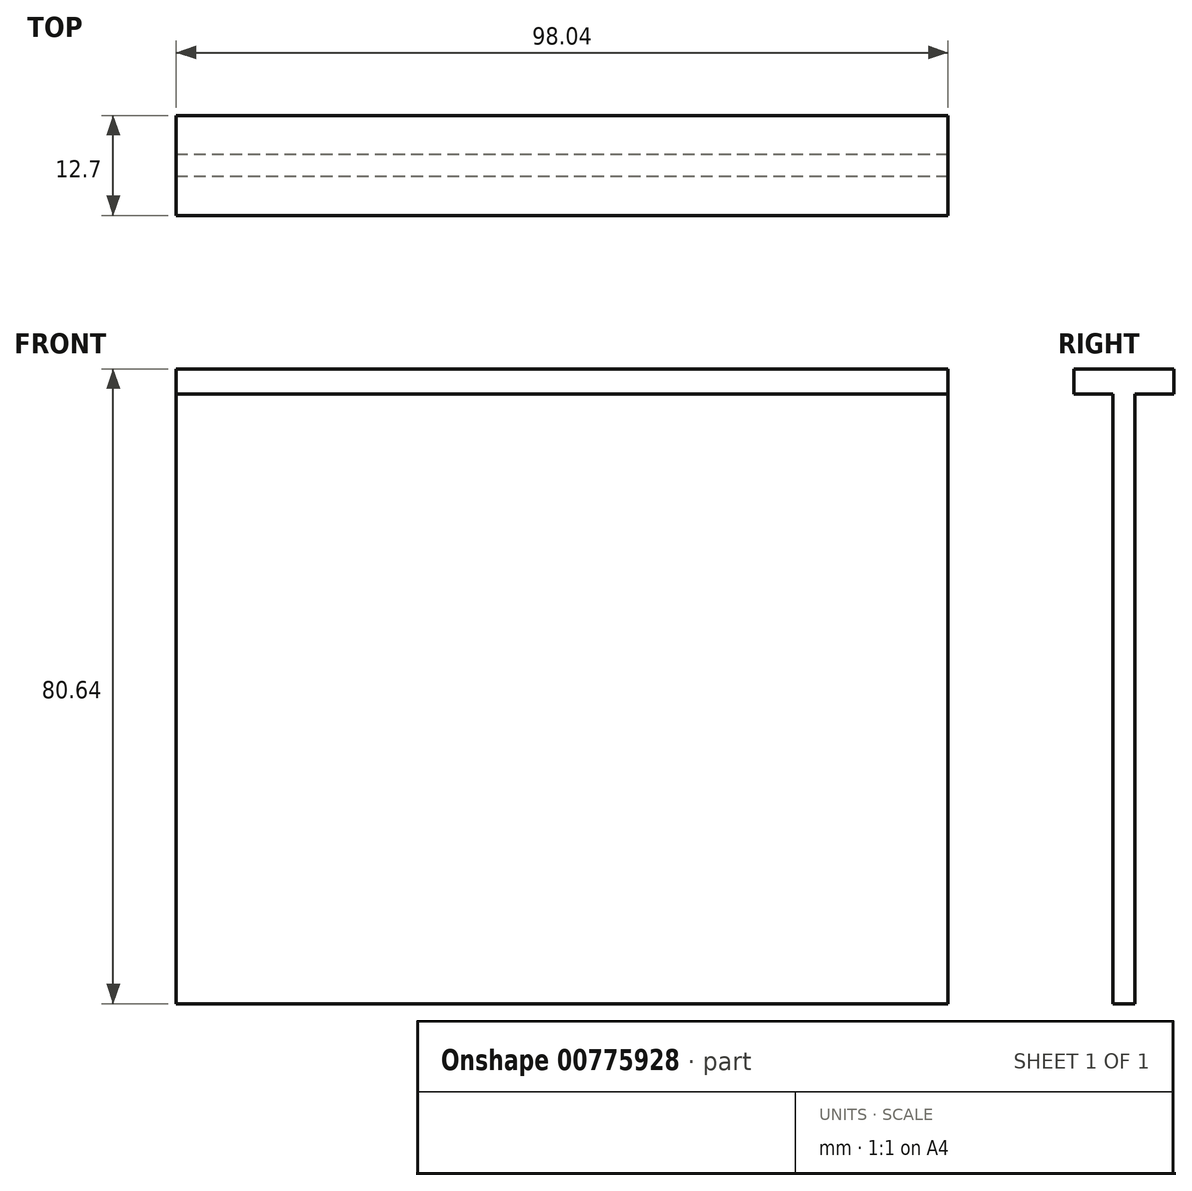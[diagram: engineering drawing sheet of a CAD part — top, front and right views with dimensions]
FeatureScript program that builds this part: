
annotation { "Feature Type Name" : "Feature", "Feature Type Description" : "" }
export const myFeature = defineFeature(function(context is Context, id is Id, definition is map)
    precondition{}
    {
        {
            var Q0;
            Q0=qCreatedBy(makeId("Right.planeOp"),FACE);
            var sketch = newSketch(context, id + "F0", { "sketchPlane" : qUnion([Q0])});
            skLineSegment(sketch, "E0", {"start": v(0, 0) * mm, "end": v(0, 3.17) * mm});
            skLineSegment(sketch, "E1", {"start": v(0, 3.17) * mm, "end": v(12.7, 3.17) * mm});
            skLineSegment(sketch, "E2", {"start": v(12.7, 3.17) * mm, "end": v(12.7, 0) * mm});
            skLineSegment(sketch, "E3", {"start": v(12.7, 0) * mm, "end": v(7.75, 0) * mm});
            skLineSegment(sketch, "E4", {"start": v(7.75, 0) * mm, "end": v(7.75, -77.47) * mm});
            skLineSegment(sketch, "E5", {"start": v(7.75, -77.47) * mm, "end": v(4.95, -77.47) * mm});
            skLineSegment(sketch, "E6", {"start": v(4.95, -77.47) * mm, "end": v(4.95, 0) * mm});
            skLineSegment(sketch, "E7", {"start": v(4.95, 0) * mm, "end": v(0, 0) * mm});
            skSolve(sketch);
        }
        {
            var Q0;
            Q0 = qSketchRegion(id + "F0", true);
            extrude(context, id + "F1", {"entities" : qUnion([Q0]), "depth" : 98.04 * mm, "offsetDistance" : 25.4 * mm});
        }
    });
